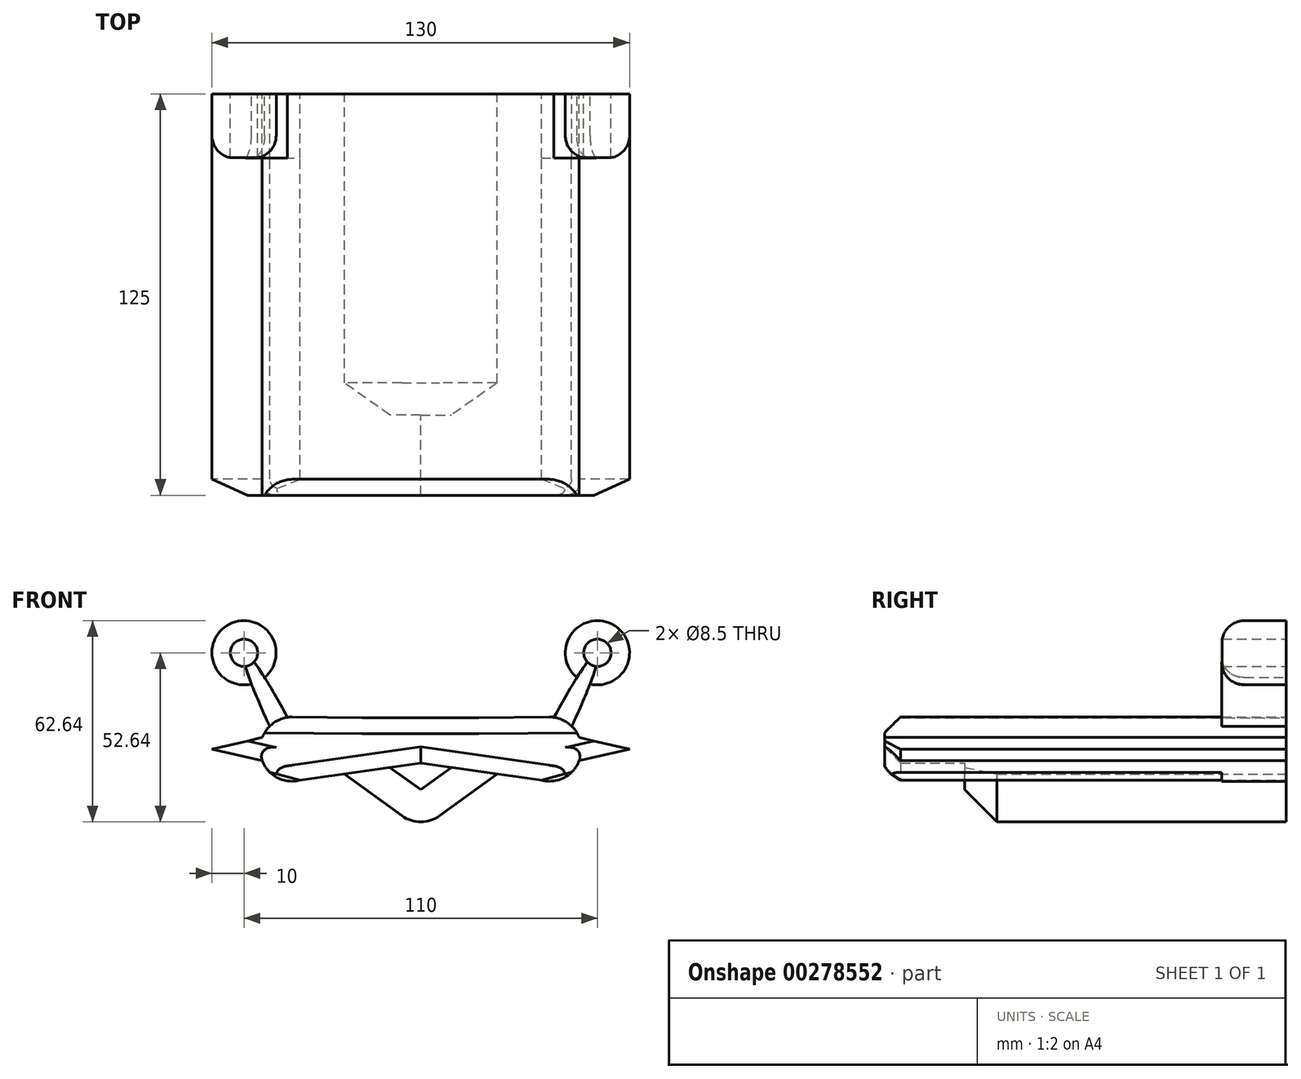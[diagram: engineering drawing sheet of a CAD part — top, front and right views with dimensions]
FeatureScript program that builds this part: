
annotation { "Feature Type Name" : "Feature", "Feature Type Description" : "" }
export const myFeature = defineFeature(function(context is Context, id is Id, definition is map)
    precondition{}
    {
        {
            var Q0;
            Q0=qCreatedBy(makeId("Front.planeOp"),FACE);
            var sketch = newSketch(context, id + "F0", { "sketchPlane" : qUnion([Q0])});
            skCircle(sketch, "E0.cCircle", {"center": v(0, 0) * mm, "radius": 20.23 * mm, "construction": true});
            skLineSegment(sketch, "E0.0", {"start": v(23.78, -7.73) * mm, "end": v(0, -25) * mm});
            skLineSegment(sketch, "E0.1", {"start": v(0, -25) * mm, "end": v(-23.78, -7.73) * mm});
            skLineSegment(sketch, "E1", {"start": v(0, 0) * mm, "end": v(-40, 0) * mm, "construction": true});
            skArc(sketch, "E2", {"start": v(-39.82, 10) * mm, "mid": v(-45.57, 8.3) * mm, "end": v(-49.32, 3.62) * mm});
            skLineSegment(sketch, "E3", {"start": v(-23.78, -7.73) * mm, "end": v(-37.55, -9.7) * mm});
            skLineSegment(sketch, "E4", {"start": v(-40, 0) * mm, "end": v(-40, 10) * mm, "construction": true});
            skLineSegment(sketch, "E5", {"start": v(-40, 10) * mm, "end": v(-18.08, 9.8) * mm});
            skLineSegment(sketch, "E6", {"start": v(-18.08, 9.8) * mm, "end": v(-17.7, 9.8) * mm});
            skPoint(sketch, "E7.orphan", {"position": v(0, 9.63) * mm});
            skPoint(sketch, "E8.orphan", {"position": v(-14.7, 20.23) * mm});
            skPoint(sketch, "E9.orphan", {"position": v(14.7, 20.23) * mm});
            skLineSegment(sketch, "E10.MirrorCS", {"start": v(40, 10) * mm, "end": v(18.08, 9.8) * mm});
            skArc(sketch, "E11.MirrorCS", {"start": v(39.82, 10) * mm, "mid": v(45.57, 8.3) * mm, "end": v(49.32, 3.62) * mm});
            skLineSegment(sketch, "E12.MirrorCS", {"start": v(23.78, -7.73) * mm, "end": v(37.55, -9.7) * mm});
            skLineSegment(sketch, "E13", {"start": v(-18.08, 9.8) * mm, "end": v(18.08, 9.8) * mm});
            skLineSegment(sketch, "E14", {"start": v(-37.55, -9.7) * mm, "end": v(-32.3, -21.25) * mm});
            skLineSegment(sketch, "E15", {"start": v(-32.3, -21.25) * mm, "end": v(-46.93, -7.21) * mm});
            skLineSegment(sketch, "E16.MirrorCS", {"start": v(37.55, -9.7) * mm, "end": v(32.3, -21.25) * mm});
            skLineSegment(sketch, "E17.MirrorCS", {"start": v(32.3, -21.25) * mm, "end": v(46.93, -7.21) * mm});
            skPoint(sketch, "E18.orphan", {"position": v(37.55, -9.7) * mm});
            skLineSegment(sketch, "E19", {"start": v(-49.32, 3.62) * mm, "end": v(-65, 0) * mm});
            skLineSegment(sketch, "E20", {"start": v(-65, 0) * mm, "end": v(-49.32, -3.62) * mm});
            skLineSegment(sketch, "E21.MirrorCS", {"start": v(49.32, 3.62) * mm, "end": v(65, 0) * mm});
            skLineSegment(sketch, "E22.MirrorCS", {"start": v(65, 0) * mm, "end": v(49.32, -3.62) * mm});
            skArc(sketch, "E23.trimOffspring", {"start": v(-49.32, -3.62) * mm, "mid": v(-48.32, -5.55) * mm, "end": v(-46.93, -7.21) * mm});
            skArc(sketch, "E24.trimOffspring", {"start": v(49.32, -3.62) * mm, "mid": v(48.32, -5.55) * mm, "end": v(46.93, -7.21) * mm});
            skLineSegment(sketch, "E25", {"start": v(-46.93, -7.21) * mm, "end": v(-37.55, -9.7) * mm});
            skLineSegment(sketch, "E26", {"start": v(37.55, -9.7) * mm, "end": v(46.93, -7.21) * mm});
            skSolve(sketch);
        }
        {
            var Q0;
            Q0=makeQuery(id+"F0.imprint","IMPRINT",FACE,{"disambiguationData":[TD([[makeQuery(id+"F0.imprint","IMPRINT",EDGE,{"derivedFrom":sQuery(id+"F0.wireOp",EDGE,"E0.0")}),-1.0]])]});
            extrude(context, id + "F1", {"entities" : qUnion([Q0]), "depth" : 50 * mm, "hasSecondDirection" : true, "secondDirectionOppositeDirection" : true, "secondDirectionDepth" : 50 * mm});
        }
        {
            var Q0;
            Q0=qCreatedBy(makeId("Front.planeOp"),FACE);
            cPlane(context, id + "F2", {"entities" : qUnion([Q0]), "cplaneType" : CPlaneType.OFFSET, "offset" : 50 * mm, "oppositeDirection" : true, "width" : 150 * mm, "height" : 150 * mm});
        }
        {
            var Q0;
            Q0=qCreatedBy(id+"F2.planeOp",FACE);
            var sketch = newSketch(context, id + "F3", { "sketchPlane" : qUnion([Q0])});
            skPoint(sketch, "E27", {"position": v(0, 0) * mm});
            skPoint(sketch, "E28", {"position": v(-40, 0) * mm});
            skPoint(sketch, "E29.MirrorP", {"position": v(40, 0) * mm});
            skSolve(sketch);
        }
        {
            var Q0;
            Q0=qCreatedBy(id+"F2.planeOp",FACE);
            var sketch = newSketch(context, id + "F4", { "sketchPlane" : qUnion([Q0])});
            skCircle(sketch, "E30", {"center": v(-55, 30) * mm, "radius": 52.5 * mm, "construction": true});
            skCircle(sketch, "E31", {"center": v(-55, 30) * mm, "radius": 4.25 * mm});
            skArc(sketch, "E32", {"start": v(-48.6, 22.31) * mm, "mid": v(-59.47, 38.94) * mm, "end": v(-52.68, 20.27) * mm});
            skLineSegment(sketch, "E33", {"start": v(-55, 30) * mm, "end": v(-40, 0) * mm, "construction": true});
            skEllipticalArc(sketch, "E34", {});
            skLineSegment(sketch, "E35", {"start": v(-36.39, 0) * mm, "end": v(-43.61, 0) * mm});
            skEllipticalArc(sketch, "E36.trimOffspring", {});
            skArc(sketch, "E37.MirrorCS", {"start": v(48.6, 22.31) * mm, "mid": v(59.47, 38.94) * mm, "end": v(52.68, 20.27) * mm});
            skCircle(sketch, "E38.MirrorC", {"center": v(55, 30) * mm, "radius": 4.25 * mm});
            skEllipticalArc(sketch, "E39.MirrorCS", {});
            skEllipticalArc(sketch, "E40.MirrorCS", {});
            skLineSegment(sketch, "E41.MirrorCS", {"start": v(36.39, 0) * mm, "end": v(43.61, 0) * mm});
            skCircle(sketch, "E42", {"center": v(-40, 0) * mm, "radius": 10 * mm});
            skCircle(sketch, "E43.MirrorC", {"center": v(40, 0) * mm, "radius": 10 * mm});
            skPoint(sketch, "E44.orphan", {"position": v(43.61, 0) * mm});
            skPoint(sketch, "E45.orphan", {"position": v(36.39, 0) * mm});
            const initialGuessF4  = {"E34": [-0.04, 0, -0.4472135954999579, 0.894427190999916, 0.03354101966249685, 0.0032362267526245426, 4.999748035327611, 5.501474979849175], "E36.trimOffspring": [-0.04, 0, -0.4472135954999579, 0.894427190999916, 0.03354101966249685, 0.0032362267526245426, 0.7817103273304103, 1.2834372718519744], "E39.MirrorCS": [0.04, 0, 0.4472135954999579, 0.894427190999916, 0.03354101966249685, 0.0032362267526245426, 4.999748035327611, 5.501474979849176], "E40.MirrorCS": [0.04, 0, 0.4472135954999579, 0.894427190999916, 0.03354101966249685, 0.0032362267526245426, 0.7817103273304109, 1.2834372718519753]};
            skSetInitialGuess(sketch, initialGuessF4);
            skSolve(sketch);
        }
        {
            var Q0;
            Q0=makeQuery(id+"F1.opExtrude","SWEPT_EDGE",EDGE,{"disambiguationData":[OSD([sQuery(id+"F0.wireOp",EDGE,"E0.0"),sQuery(id+"F0.wireOp",EDGE,"E0.1")])]});
            var Q1;
            Q1=makeQuery(id+"FCDHG0mXteZjTb6_1.opLoft","SWEPT_EDGE",EDGE,{"disambiguationData":[OSD([sQuery(id+"F0.wireOp",EDGE,"E0.0"),sQuery(id+"F0.wireOp",EDGE,"E0.1"),sQuery(id+"F3.wireOp",VERTEX,"E27")])]});
            fillet(context, id + "F5", {"entities" : qUnion([Q0, Q1]), "radius" : 10 * mm, "tangentPropagation" : true, "allowEdgeOverflow" : false});
        }
        {
            var Q0;
            Q0 = qSketchRegion(id + "F4", true);
            extrude(context, id + "F6", {"entities" : qUnion([Q0]), "operationType" : NewBodyOperationType.ADD, "depth" : 20 * mm});
        }
        {
            var Q0;
            Q0=makeQuery(id+"F1.opExtrude","CAP_FACE",FACE,{"disambiguationData":[OSD([sQuery(id+"F0.wireOp",EDGE,"E0.0"),sQuery(id+"F0.wireOp",EDGE,"E0.1"),sQuery(id+"F0.wireOp",EDGE,"E2"),sQuery(id+"F0.wireOp",EDGE,"E3"),sQuery(id+"F0.wireOp",EDGE,"E5"),sQuery(id+"F0.wireOp",EDGE,"E10.MirrorCS"),sQuery(id+"F0.wireOp",EDGE,"E11.MirrorCS"),sQuery(id+"F0.wireOp",EDGE,"E12.MirrorCS"),sQuery(id+"F0.wireOp",EDGE,"E13"),sQuery(id+"F0.wireOp",EDGE,"E14"),sQuery(id+"F0.wireOp",EDGE,"E15"),sQuery(id+"F0.wireOp",EDGE,"E16.MirrorCS"),sQuery(id+"F0.wireOp",EDGE,"E17.MirrorCS"),sQuery(id+"F0.wireOp",EDGE,"E19"),sQuery(id+"F0.wireOp",EDGE,"E20"),sQuery(id+"F0.wireOp",EDGE,"E21.MirrorCS"),sQuery(id+"F0.wireOp",EDGE,"E22.MirrorCS"),sQuery(id+"F0.wireOp",EDGE,"E23.trimOffspring"),sQuery(id+"F0.wireOp",EDGE,"E24.trimOffspring")])],"isStart":false});
            var sketch = newSketch(context, id + "F7", { "sketchPlane" : qUnion([Q0])});
            skArc(sketch, "E46", {"start": v(-49.32, -3.62) * mm, "mid": v(-44.59, -8.89) * mm, "end": v(-37.55, -9.7) * mm});
            skLineSegment(sketch, "E47", {"start": v(-65, 0) * mm, "end": v(-49.32, 3.62) * mm});
            skLineSegment(sketch, "E48", {"start": v(-65, 0) * mm, "end": v(-49.32, -3.62) * mm});
            skLineSegment(sketch, "E49", {"start": v(-40, 10) * mm, "end": v(0, 10) * mm});
            skLineSegment(sketch, "E50", {"start": v(-37.55, -9.7) * mm, "end": v(0, -4.32) * mm});
            skArc(sketch, "E51.trimOffspring", {"start": v(-40, 10) * mm, "mid": v(-45.65, 8.25) * mm, "end": v(-49.32, 3.62) * mm});
            skArc(sketch, "E52.MirrorCS", {"start": v(49.32, -3.62) * mm, "mid": v(44.59, -8.89) * mm, "end": v(37.55, -9.7) * mm});
            skArc(sketch, "E53.MirrorCS", {"start": v(40, 10) * mm, "mid": v(45.65, 8.25) * mm, "end": v(49.32, 3.62) * mm});
            skLineSegment(sketch, "E54.MirrorCS", {"start": v(37.55, -9.7) * mm, "end": v(0, -4.32) * mm});
            skLineSegment(sketch, "E55.MirrorCS", {"start": v(65, 0) * mm, "end": v(49.32, -3.62) * mm});
            skLineSegment(sketch, "E56.MirrorCS", {"start": v(40, 10) * mm, "end": v(0, 10) * mm});
            skLineSegment(sketch, "E57.MirrorCS", {"start": v(65, 0) * mm, "end": v(49.32, 3.62) * mm});
            skSolve(sketch);
        }
        {
            var Q0;
            Q0=makeQuery(id+"F7.imprint","IMPRINT",FACE,{"disambiguationData":[TD([[makeQuery(id+"F7.imprint","IMPRINT",EDGE,{"derivedFrom":sQuery(id+"F7.wireOp",EDGE,"E47")}),1.0]])]});
            extrude(context, id + "F8", {"entities" : qUnion([Q0]), "operationType" : NewBodyOperationType.ADD, "depth" : 25 * mm});
        }
        {
            var Q0;
            Q0=makeQuery(id+"F1.opExtrude","CAP_EDGE",EDGE,{"disambiguationData":[OSD([sQuery(id+"F0.wireOp",EDGE,"E0.1")])],"isStart":false});
            var Q1;
            {var subQ0=sQuery(id+"F0.wireOp",EDGE,"E0.1");var subQ1=sQuery(id+"F0.wireOp",EDGE,"E0.0");Q1=makeQuery(id+"F5.opFillet","BLEND_EDGE",EDGE,{"blendedFrom":[makeQuery(id+"F1.opExtrude","SWEPT_EDGE",EDGE,{"disambiguationData":[OSD([subQ1,subQ0])]}),makeQuery(id+"F1.opExtrude","CAP_FACE",FACE,{"disambiguationData":[OSD([subQ1,subQ0,sQuery(id+"F0.wireOp",EDGE,"E2"),sQuery(id+"F0.wireOp",EDGE,"E3"),sQuery(id+"F0.wireOp",EDGE,"E5"),sQuery(id+"F0.wireOp",EDGE,"E10.MirrorCS"),sQuery(id+"F0.wireOp",EDGE,"E11.MirrorCS"),sQuery(id+"F0.wireOp",EDGE,"E12.MirrorCS"),sQuery(id+"F0.wireOp",EDGE,"E13"),sQuery(id+"F0.wireOp",EDGE,"E14"),sQuery(id+"F0.wireOp",EDGE,"E15"),sQuery(id+"F0.wireOp",EDGE,"E16.MirrorCS"),sQuery(id+"F0.wireOp",EDGE,"E17.MirrorCS"),sQuery(id+"F0.wireOp",EDGE,"E19"),sQuery(id+"F0.wireOp",EDGE,"E20"),sQuery(id+"F0.wireOp",EDGE,"E21.MirrorCS"),sQuery(id+"F0.wireOp",EDGE,"E22.MirrorCS"),sQuery(id+"F0.wireOp",EDGE,"E23.trimOffspring"),sQuery(id+"F0.wireOp",EDGE,"E24.trimOffspring")])],"isStart":false})],"blendedInto":[makeQuery(id+"F1.opExtrude","CAP_FACE",FACE,{"disambiguationData":[OSD([subQ1,subQ0,sQuery(id+"F0.wireOp",EDGE,"E2"),sQuery(id+"F0.wireOp",EDGE,"E3"),sQuery(id+"F0.wireOp",EDGE,"E5"),sQuery(id+"F0.wireOp",EDGE,"E10.MirrorCS"),sQuery(id+"F0.wireOp",EDGE,"E11.MirrorCS"),sQuery(id+"F0.wireOp",EDGE,"E12.MirrorCS"),sQuery(id+"F0.wireOp",EDGE,"E13"),sQuery(id+"F0.wireOp",EDGE,"E14"),sQuery(id+"F0.wireOp",EDGE,"E15"),sQuery(id+"F0.wireOp",EDGE,"E16.MirrorCS"),sQuery(id+"F0.wireOp",EDGE,"E17.MirrorCS"),sQuery(id+"F0.wireOp",EDGE,"E19"),sQuery(id+"F0.wireOp",EDGE,"E20"),sQuery(id+"F0.wireOp",EDGE,"E21.MirrorCS"),sQuery(id+"F0.wireOp",EDGE,"E22.MirrorCS"),sQuery(id+"F0.wireOp",EDGE,"E23.trimOffspring"),sQuery(id+"F0.wireOp",EDGE,"E24.trimOffspring")])],"isStart":false})]});}
            var Q2;
            Q2=makeQuery(id+"F1.opExtrude","CAP_EDGE",EDGE,{"disambiguationData":[OSD([sQuery(id+"F0.wireOp",EDGE,"E0.0")])],"isStart":false});
            chamfer(context, id + "F9", {"entities" : qUnion([Q0, Q1, Q2]), "width" : 10 * mm, "tangentPropagation" : true});
        }
        {
            var Q0;
            Q0=makeQuery(id+"F8.opExtrude","CAP_EDGE",EDGE,{"disambiguationData":[OSD([sQuery(id+"F7.wireOp",EDGE,"E50")])],"isStart":false});
            var Q1;
            Q1=makeQuery(id+"F8.opExtrude","CAP_EDGE",EDGE,{"disambiguationData":[OSD([sQuery(id+"F7.wireOp",EDGE,"E54.MirrorCS")])],"isStart":false});
            var Q2;
            Q2=makeQuery(id+"F8.opExtrude","CAP_EDGE",EDGE,{"disambiguationData":[OSD([sQuery(id+"F0.wireOp",EDGE,"E10.MirrorCS")])],"isStart":false});
            var Q3;
            Q3=makeQuery(id+"F8.opExtrude","CAP_EDGE",EDGE,{"disambiguationData":[OSD([sQuery(id+"F0.wireOp",EDGE,"E13")])],"isStart":false});
            var Q4;
            Q4=makeQuery(id+"F8.opExtrude","CAP_EDGE",EDGE,{"disambiguationData":[OSD([sQuery(id+"F0.wireOp",EDGE,"E5")])],"isStart":false});
            var Q5;
            Q5=makeQuery(id+"F8.opExtrude","CAP_EDGE",EDGE,{"disambiguationData":[OSD([sQuery(id+"F7.wireOp",EDGE,"E55.MirrorCS")])],"isStart":false});
            var Q6;
            Q6=makeQuery(id+"F8.opExtrude","CAP_EDGE",EDGE,{"disambiguationData":[OSD([sQuery(id+"F7.wireOp",EDGE,"E48")])],"isStart":false});
            chamfer(context, id + "F10", {"entities" : qUnion([Q0, Q1, Q2, Q3, Q4, Q5, Q6]), "width" : 5 * mm, "tangentPropagation" : true});
        }
        {
            var Q0;
            Q0=makeQuery(id+"F8.opExtrude","CAP_EDGE",EDGE,{"disambiguationData":[OSD([sQuery(id+"F7.wireOp",EDGE,"E46")])],"isStart":false});
            var Q1;
            Q1=makeQuery(id+"F8.opExtrude","CAP_EDGE",EDGE,{"disambiguationData":[OSD([sQuery(id+"F7.wireOp",EDGE,"E52.MirrorCS")])],"isStart":false});
            fillet(context, id + "F11", {"entities" : qUnion([Q0, Q1]), "radius" : 5 * mm, "tangentPropagation" : true, "allowEdgeOverflow" : false});
        }
        {
            var Q0;
            Q0=makeQuery(id+"F6.opExtrude","CAP_EDGE",EDGE,{"disambiguationData":[OSD([sQuery(id+"F4.wireOp",EDGE,"E37.MirrorCS")])],"isStart":false});
            var Q1;
            Q1=makeQuery(id+"F6.opExtrude","CAP_EDGE",EDGE,{"disambiguationData":[OSD([sQuery(id+"F4.wireOp",EDGE,"E32")])],"isStart":false});
            fillet(context, id + "F12", {"entities" : qUnion([Q0, Q1]), "radius" : 7 * mm, "tangentPropagation" : true, "allowEdgeOverflow" : false});
        }
    });
